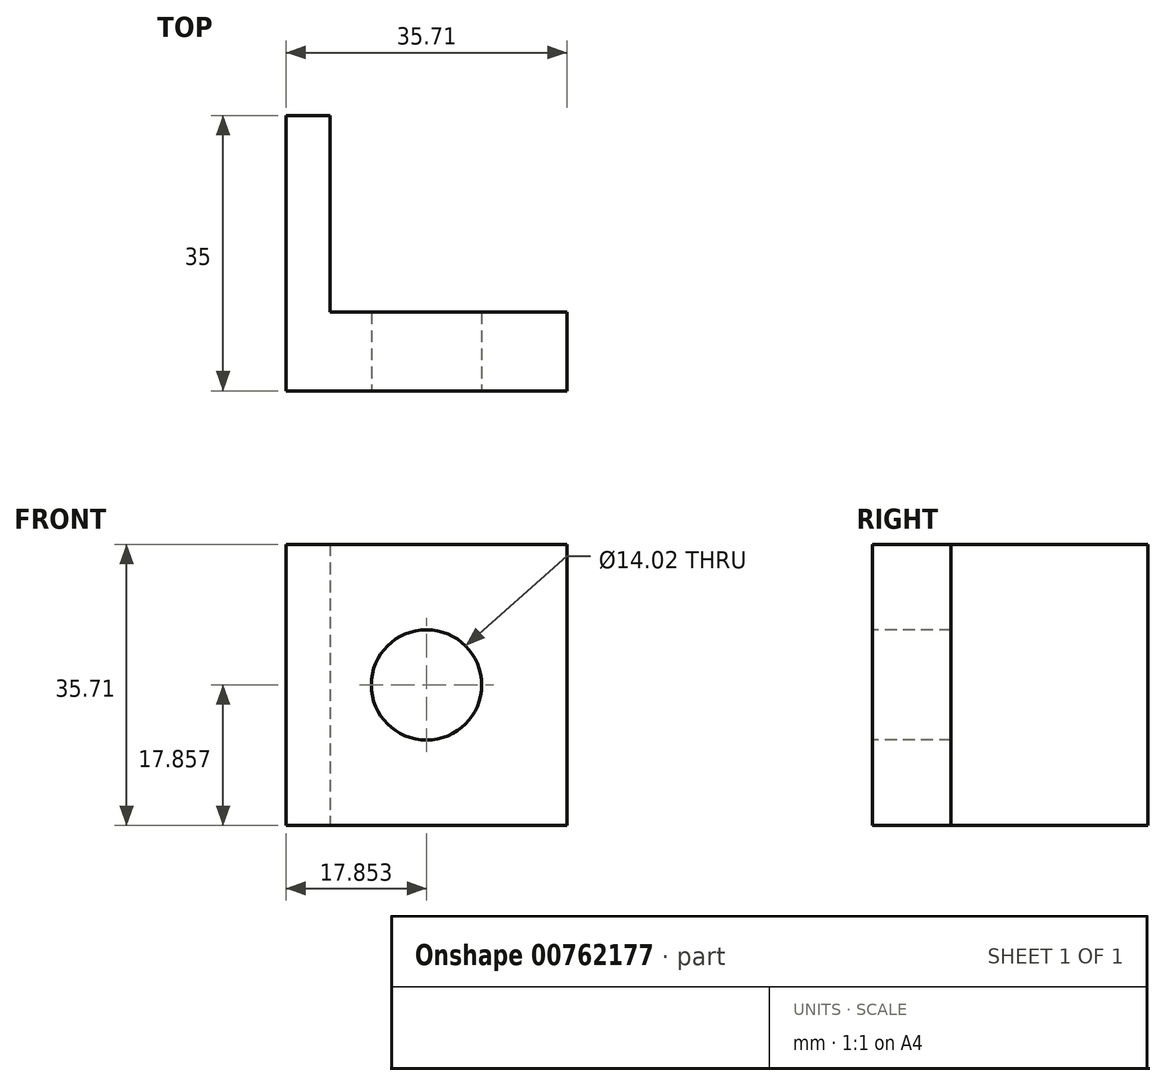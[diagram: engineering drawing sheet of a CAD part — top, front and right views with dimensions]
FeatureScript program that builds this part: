
annotation { "Feature Type Name" : "Feature", "Feature Type Description" : "" }
export const myFeature = defineFeature(function(context is Context, id is Id, definition is map)
    precondition{}
    {
        {
            var Q0;
            Q0=qCreatedBy(makeId("Front.planeOp"),FACE);
            var sketch = newSketch(context, id + "F0", { "sketchPlane" : qUnion([Q0])});
            skLineSegment(sketch, "E0.bottom", {"start": v(0, 0) * mm, "end": v(-35.71, 0) * mm});
            skLineSegment(sketch, "E0.top", {"start": v(0, 35.71) * mm, "end": v(-35.71, 35.71) * mm});
            skLineSegment(sketch, "E0.left", {"start": v(0, 0) * mm, "end": v(0, 35.71) * mm});
            skLineSegment(sketch, "E0.right", {"start": v(-35.71, 0) * mm, "end": v(-35.71, 35.71) * mm});
            skSolve(sketch);
        }
        {
            var Q0;
            Q0 = qSketchRegion(id + "F0", true);
            extrude(context, id + "F1", {"entities" : qUnion([Q0]), "depth" : 10 * mm, "offsetDistance" : 25 * mm});
        }
        {
            var Q0;
            Q0=makeQuery(id+"F1.opExtrude","CAP_FACE",FACE,{"disambiguationData":[OSD([sQuery(id+"F0.wireOp",EDGE,"E0.bottom"),sQuery(id+"F0.wireOp",EDGE,"E0.top"),sQuery(id+"F0.wireOp",EDGE,"E0.left"),sQuery(id+"F0.wireOp",EDGE,"E0.right")])],"isStart":false});
            var sketch = newSketch(context, id + "F2", { "sketchPlane" : qUnion([Q0])});
            skCircle(sketch, "E1", {"center": v(-17.86, 17.86) * mm, "radius": 7 * mm});
            skPoint(sketch, "E1.centerSnap0", {"position": v(-35.71, 17.86) * mm});
            skPoint(sketch, "E1.centerSnap1", {"position": v(-17.86, 35.71) * mm});
            skSolve(sketch);
        }
        {
            var Q0;
            Q0=makeQuery(id+"F2.imprint","IMPRINT",FACE,{"disambiguationData":[TD([[makeQuery(id+"F2.imprint","IMPRINT",EDGE,{"derivedFrom":sQuery(id+"F2.wireOp",EDGE,"E1")}),1.0]])]});
            extrude(context, id + "F3", {"entities" : qUnion([Q0]), "operationType" : NewBodyOperationType.REMOVE, "oppositeDirection" : true, "depth" : 25 * mm, "offsetDistance" : 25 * mm});
        }
        {
            var Q0;
            Q0=makeQuery(id+"F1.opExtrude","CAP_FACE",FACE,{"disambiguationData":[OSD([sQuery(id+"F0.wireOp",EDGE,"E0.bottom"),sQuery(id+"F0.wireOp",EDGE,"E0.top"),sQuery(id+"F0.wireOp",EDGE,"E0.left"),sQuery(id+"F0.wireOp",EDGE,"E0.right")])],"isStart":true});
            var sketch = newSketch(context, id + "F4", { "sketchPlane" : qUnion([Q0])});
            skLineSegment(sketch, "E2", {"start": v(30.14, 35.71) * mm, "end": v(30.14, 0) * mm});
            skSolve(sketch);
        }
        {
            var Q0;
            {var subQ0=sQuery(id+"F4.wireOp",EDGE,"E2");Q0=makeQuery(id+"F4.imprint","IMPRINT",FACE,{"disambiguationData":[TD([[makeQuery(id+"F4.imprint","IMPRINT",EDGE,{"derivedFrom":subQ0}),1.0]])]});}
            extrude(context, id + "F5", {"entities" : qUnion([Q0]), "operationType" : NewBodyOperationType.ADD, "depth" : 25 * mm, "offsetDistance" : 25 * mm});
        }
    });
